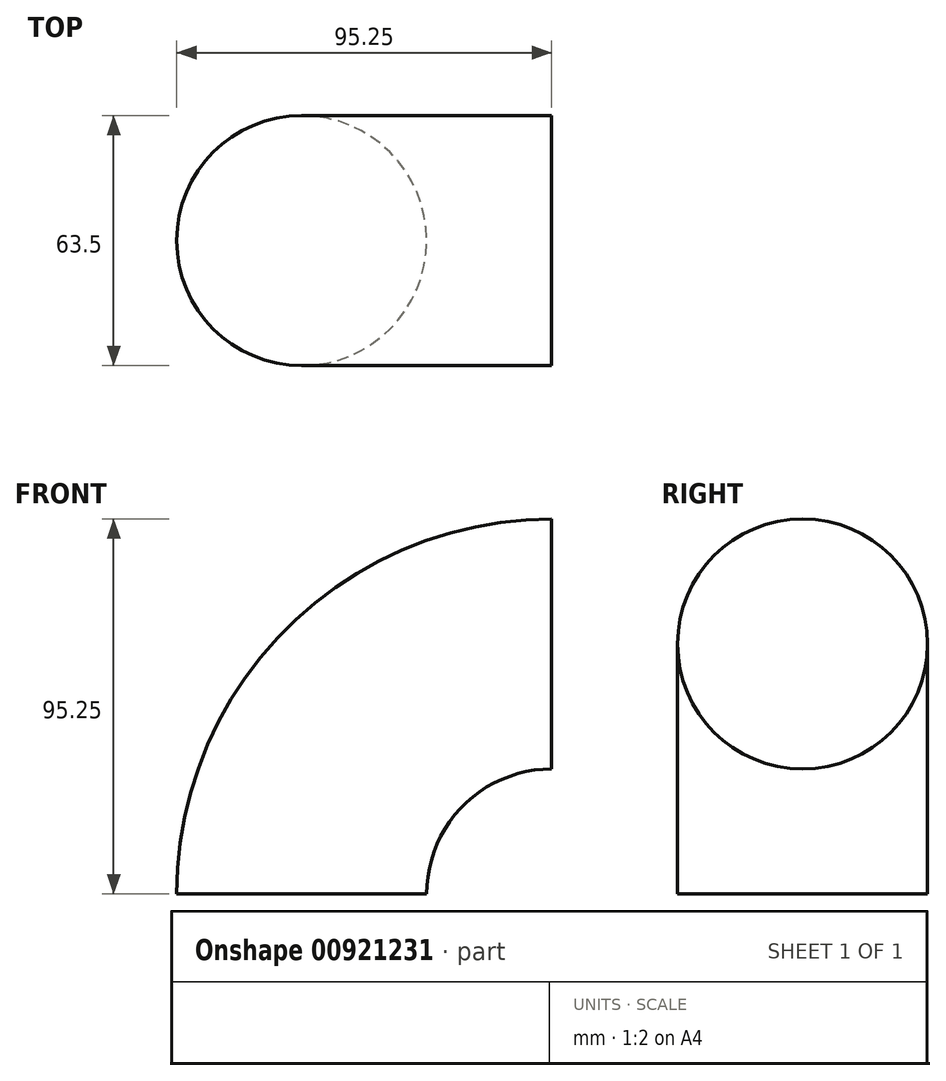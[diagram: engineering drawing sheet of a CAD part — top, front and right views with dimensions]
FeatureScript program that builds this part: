
annotation { "Feature Type Name" : "Feature", "Feature Type Description" : "" }
export const myFeature = defineFeature(function(context is Context, id is Id, definition is map)
    precondition{}
    {
        {
            var Q0;
            Q0=qCreatedBy(makeId("Front.planeOp"),FACE);
            var sketch = newSketch(context, id + "F0", { "sketchPlane" : qUnion([Q0])});
            skLineSegment(sketch, "E0.bottom", {"start": v(0, 0) * mm, "end": v(63.5, 0) * mm});
            skLineSegment(sketch, "E0.top", {"start": v(63.5, 63.5) * mm, "end": v(63.5, 63.5) * mm});
            skLineSegment(sketch, "E0.left", {"start": v(0, 0) * mm, "end": v(0, 0) * mm});
            skLineSegment(sketch, "E0.right", {"start": v(63.5, 0) * mm, "end": v(63.5, 63.5) * mm});
            skPoint(sketch, "E1.visualSharp", {"position": v(0, 63.5) * mm});
            skArc(sketch, "E1.filletArc", {"start": v(63.5, 63.5) * mm, "mid": v(18.6, 44.9) * mm, "end": v(0, 0) * mm});
            skPoint(sketch, "E2", {"position": v(63.5, 63.5) * mm});
            skSolve(sketch);
        }
        {
            var Q0;
            Q0=sQuery(id+"F0.wireOp",EDGE,"E1.filletArc");
            var Q1;
            Q1=qCreatedBy(makeId("Origin.pointOp"),VERTEX);
            cPlane(context, id + "F1", {"entities" : qUnion([Q0, Q1]), "cplaneType" : CPlaneType.CURVE_POINT, "offset" : 25.4 * mm, "width" : 152.4 * mm, "height" : 152.4 * mm});
        }
        {
            var Q0;
            Q0=qCreatedBy(id+"F1.planeOp",FACE);
            var sketch = newSketch(context, id + "F2", { "sketchPlane" : qUnion([Q0])});
            skCircle(sketch, "E3", {"center": v(0, 0) * mm, "radius": 31.75 * mm});
            skSolve(sketch);
        }
        {
            var Q0;
            Q0=sQuery(id+"F0.wireOp",VERTEX,"E2");
            var Q1;
            Q1=sQuery(id+"F0.wireOp",EDGE,"E1.filletArc");
            cPlane(context, id + "F3", {"entities" : qUnion([Q0, Q1]), "cplaneType" : CPlaneType.CURVE_POINT, "offset" : 25.4 * mm, "width" : 152.4 * mm, "height" : 152.4 * mm});
        }
        {
            var Q0;
            Q0=qCreatedBy(id+"F3.planeOp",FACE);
            var sketch = newSketch(context, id + "F4", { "sketchPlane" : qUnion([Q0])});
            skCircle(sketch, "E4", {"center": v(0, 63.5) * mm, "radius": 31.75 * mm});
            skSolve(sketch);
        }
        {
            var Q0;
            Q0=makeQuery(id+"F4.imprint","IMPRINT",FACE,{"disambiguationData":[TD([[makeQuery(id+"F4.imprint","IMPRINT",EDGE,{"derivedFrom":sQuery(id+"F4.wireOp",EDGE,"E4")}),1.0]])]});
            var Q1;
            Q1=makeQuery(id+"F2.imprint","IMPRINT",FACE,{"disambiguationData":[TD([[makeQuery(id+"F2.imprint","IMPRINT",EDGE,{"derivedFrom":sQuery(id+"F2.wireOp",EDGE,"E3")}),1.0]])]});
            var Q2;
            Q2=sQuery(id+"F0.wireOp",EDGE,"E1.filletArc");
            sweep(context, id + "F5", {"profiles" : qUnion([Q0, Q1]), "path" : qUnion([Q2])});
        }
    });
